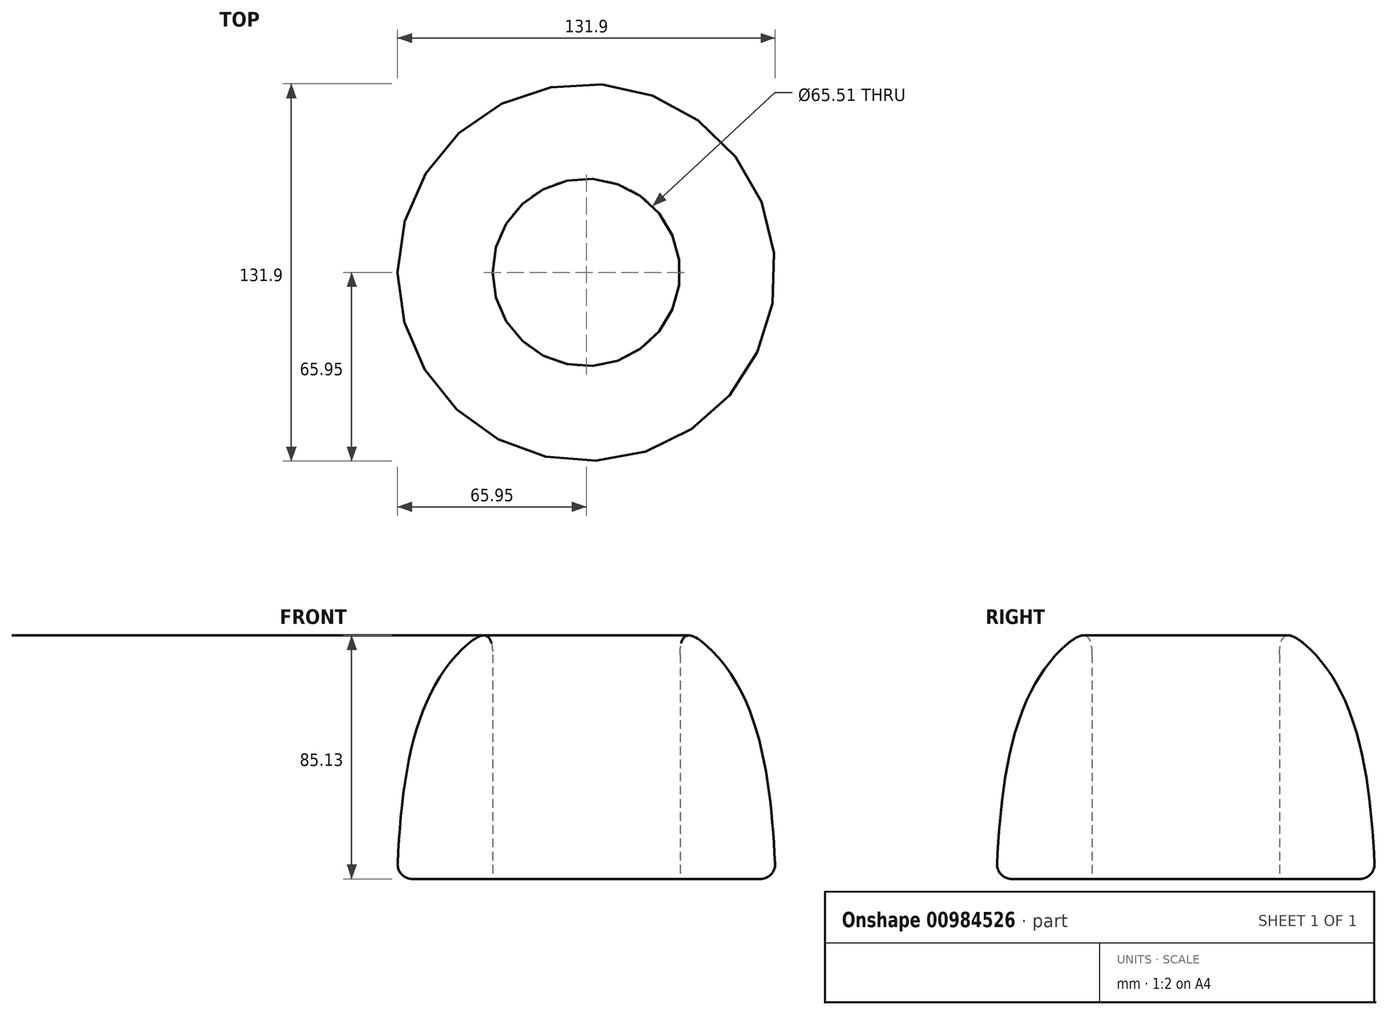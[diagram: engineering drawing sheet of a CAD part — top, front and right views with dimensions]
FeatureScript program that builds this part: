
annotation { "Feature Type Name" : "Feature", "Feature Type Description" : "" }
export const myFeature = defineFeature(function(context is Context, id is Id, definition is map)
    precondition{}
    {
        {
            var Q0;
            Q0=qCreatedBy(makeId("Front.planeOp"),FACE);
            var sketch = newSketch(context, id + "F0", { "sketchPlane" : qUnion([Q0])});
            skFitSpline(sketch, "E0", {"points": [v(-66.18, -56.06) * mm, v(-60.65, -8.56) * mm, v(-46.11, 21.43) * mm, v(-24.63, 35.59) * mm, v(0, 39.32) * mm], "startDerivative": vector(6.81, 164.5) * mm, "endDerivative": vector(116.72, 1.4) * mm});
            skLineSegment(sketch, "E1", {"start": v(-66.18, -56.06) * mm, "end": v(0, -56.06) * mm});
            skFitSpline(sketch, "E2.MirrorCS", {"points": [v(66.18, -56.06) * mm, v(60.65, -8.56) * mm, v(46.11, 21.43) * mm, v(24.63, 35.59) * mm, v(0, 39.32) * mm], "startDerivative": vector(-6.81, 164.5) * mm, "endDerivative": vector(-116.72, 1.4) * mm});
            skLineSegment(sketch, "E3.MirrorCS", {"start": v(66.18, -56.06) * mm, "end": v(0, -56.06) * mm});
            skLineSegment(sketch, "E4", {"start": v(0, 39.32) * mm, "end": v(0, -56.06) * mm});
            skSolve(sketch);
        }
        {
            var Q0;
            Q0=makeQuery(id+"F0.imprint","IMPRINT",FACE,{"disambiguationData":[TD([[makeQuery(id+"F0.imprint","IMPRINT",EDGE,{"derivedFrom":sQuery(id+"F0.wireOp",EDGE,"E0")}),-1.0]])]});
            var Q1;
            Q1=sQuery(id+"F0.wireOp",EDGE,"E4");
            revolve(context, id + "F1", {"surfaceOperationType" : NewSurfaceOperationType.NEW, "entities" : qUnion([Q0]), "axis" : qUnion([Q1]), "revolveType" : RevolveType.FULL, "oppositeDirection" : true});
        }
        {
            var Q0;
            Q0=qCreatedBy(makeId("Top.planeOp"),FACE);
            var sketch = newSketch(context, id + "F2", { "sketchPlane" : qUnion([Q0])});
            skCircle(sketch, "E5", {"center": v(0, 0) * mm, "radius": 32.75 * mm});
            skSolve(sketch);
        }
        {
            var Q0;
            Q0 = qSketchRegion(id + "F2", true);
            var Q1;
            Q1 = qSketchRegion(id + "FyJb5VjQGFGTzOf_1", true);
            extrude(context, id + "F3", {"entities" : qUnion([Q0, Q1]), "operationType" : NewBodyOperationType.REMOVE, "endBound" : BoundingType.THROUGH_ALL, "depth" : 30.48 * mm, "offsetDistance" : 25.4 * mm});
        }
        {
            var Q0;
            Q0=makeQuery(id+"F2.imprint","IMPRINT",FACE,{"disambiguationData":[TD([[makeQuery(id+"F2.imprint","IMPRINT",EDGE,{"derivedFrom":sQuery(id+"F2.wireOp",EDGE,"E5")}),1.0]])]});
            extrude(context, id + "F4", {"entities" : qUnion([Q0]), "operationType" : NewBodyOperationType.REMOVE, "endBound" : BoundingType.THROUGH_ALL, "oppositeDirection" : true, "depth" : 77.22 * mm, "offsetDistance" : 25.4 * mm});
        }
        {
            var Q0;
            Q0=makeQuery(id+"F3.boolean.opBoolean","INTERSECT",EDGE,{"derivedFrom":[makeQuery(id+"F1.opRevolve","SWEPT_FACE",FACE,{"disambiguationData":[OSD([sQuery(id+"F0.wireOp",EDGE,"E0")])]}),makeQuery(id+"F3.opExtrude","SWEPT_FACE",FACE,{"disambiguationData":[OSD([sQuery(id+"F2.wireOp",EDGE,"E5")])]})]});
            fillet(context, id + "F5", {"entities" : qUnion([Q0]), "radius" : 5.08 * mm, "tangentPropagation" : true, "rho" : 0.5, "crossSection" : FilletCrossSection.CONIC, "allowEdgeOverflow" : false});
        }
        {
            var Q0;
            Q0=makeQuery(id+"F1.opRevolve","SWEPT_EDGE",EDGE,{"disambiguationData":[OSD([sQuery(id+"F0.wireOp",EDGE,"E0"),sQuery(id+"F0.wireOp",EDGE,"E1")])]});
            fillet(context, id + "F6", {"entities" : qUnion([Q0]), "radius" : 5.08 * mm, "tangentPropagation" : true, "allowEdgeOverflow" : false});
        }
    });
